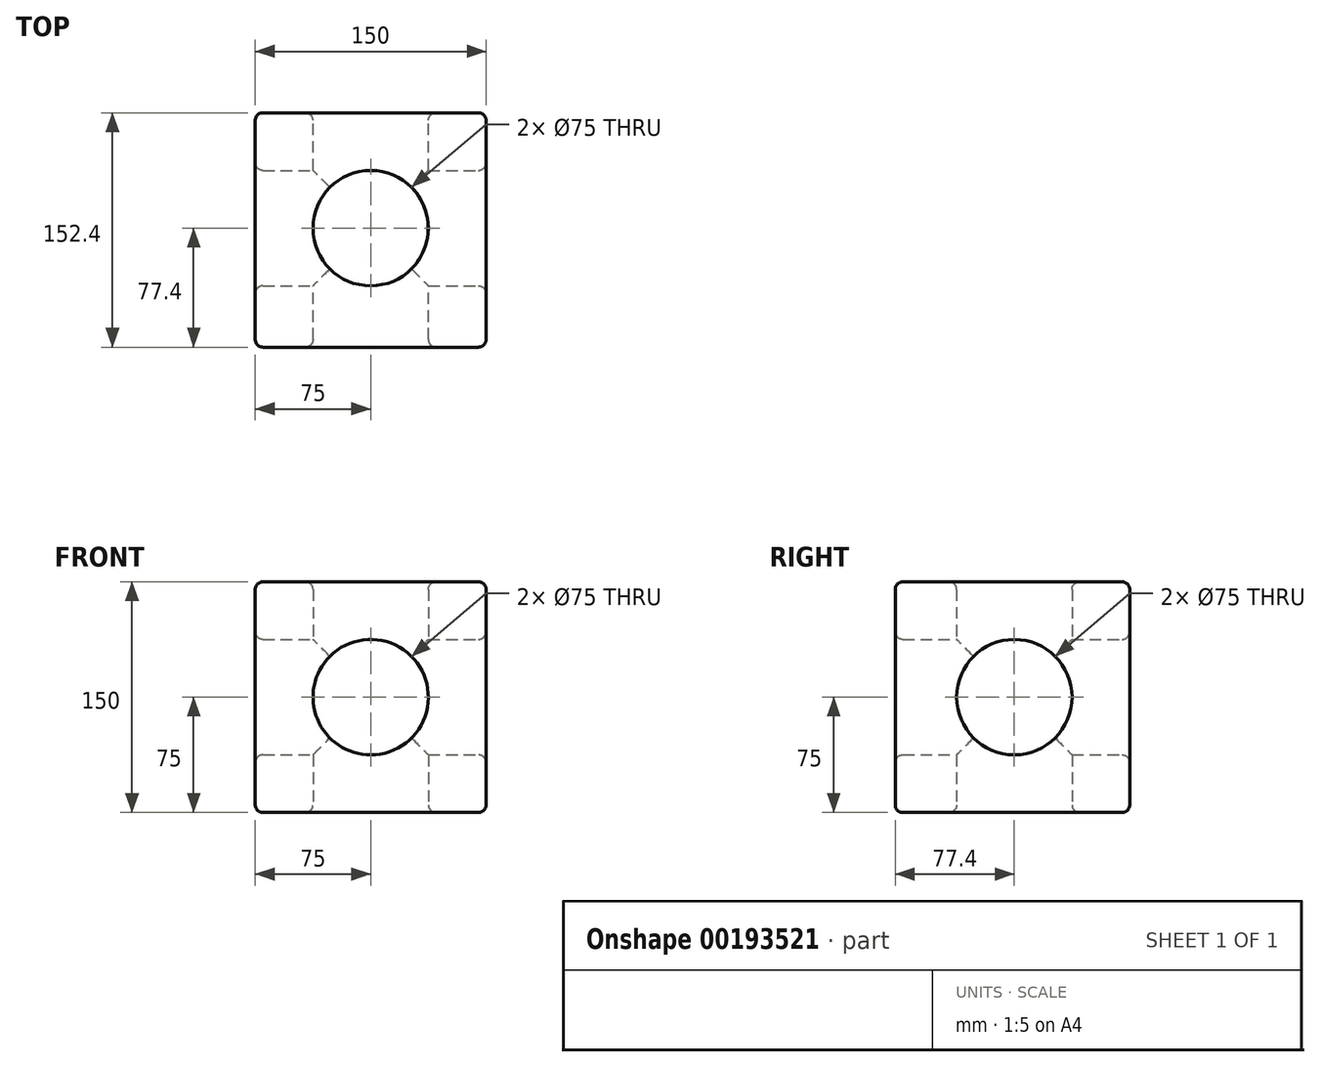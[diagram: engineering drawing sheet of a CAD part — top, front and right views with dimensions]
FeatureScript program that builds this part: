
annotation { "Feature Type Name" : "Feature", "Feature Type Description" : "" }
export const myFeature = defineFeature(function(context is Context, id is Id, definition is map)
    precondition{}
    {
        {
            var Q0;
            Q0=qCreatedBy(makeId("Front.planeOp"),FACE);
            var sketch = newSketch(context, id + "F0", { "sketchPlane" : qUnion([Q0])});
            skLineSegment(sketch, "E0.bottom", {"start": v(75, 75) * mm, "end": v(-75, 75) * mm});
            skLineSegment(sketch, "E0.top", {"start": v(75, -75) * mm, "end": v(-75, -75) * mm});
            skLineSegment(sketch, "E0.left", {"start": v(75, 75) * mm, "end": v(75, -75) * mm});
            skLineSegment(sketch, "E0.right", {"start": v(-75, 75) * mm, "end": v(-75, -75) * mm});
            skPoint(sketch, "E0.middle", {"position": v(0, 0) * mm});
            skSolve(sketch);
        }
        {
            var Q0;
            Q0=makeQuery(id+"F0.imprint","IMPRINT",FACE,{"disambiguationData":[TD([[makeQuery(id+"F0.imprint","IMPRINT",EDGE,{"derivedFrom":sQuery(id+"F0.wireOp",EDGE,"E0.bottom")}),1.0]])]});
            extrude(context, id + "F1", {"entities" : qUnion([Q0]), "depth" : 152.4 * mm});
        }
        {
            var Q0;
            Q0=makeQuery(id+"F0.imprint","IMPRINT",FACE,{"disambiguationData":[TD([[makeQuery(id+"F0.imprint","IMPRINT",EDGE,{"derivedFrom":sQuery(id+"F0.wireOp",EDGE,"E0.bottom")}),1.0]])]});
            var sketch = newSketch(context, id + "F2", { "sketchPlane" : qUnion([Q0])});
            skCircle(sketch, "E1", {"center": v(0, 0) * mm, "radius": 37.5 * mm});
            skSolve(sketch);
        }
        {
            var Q0;
            Q0 = qSketchRegion(id + "F2", true);
            extrude(context, id + "F3", {"entities" : qUnion([Q0]), "operationType" : NewBodyOperationType.REMOVE, "depth" : 252 * mm});
        }
        {
            var Q0;
            Q0=makeQuery(id+"F1.opExtrude","SWEPT_FACE",FACE,{"disambiguationData":[OSD([sQuery(id+"F0.wireOp",EDGE,"E0.top")])]});
            var sketch = newSketch(context, id + "F4", { "sketchPlane" : qUnion([Q0])});
            skCircle(sketch, "E2", {"center": v(0, 75) * mm, "radius": 37.5 * mm});
            skSolve(sketch);
        }
        {
            var Q0;
            Q0 = qSketchRegion(id + "F4", true);
            extrude(context, id + "F5", {"entities" : qUnion([Q0]), "operationType" : NewBodyOperationType.REMOVE, "oppositeDirection" : true, "depth" : 150 * mm});
        }
        {
            var Q0;
            Q0=makeQuery(id+"F1.opExtrude","SWEPT_FACE",FACE,{"disambiguationData":[OSD([sQuery(id+"F0.wireOp",EDGE,"E0.left")])]});
            var sketch = newSketch(context, id + "F6", { "sketchPlane" : qUnion([Q0])});
            skCircle(sketch, "E3", {"center": v(-75, 0) * mm, "radius": 37.5 * mm});
            skSolve(sketch);
        }
        {
            var Q0;
            Q0=makeQuery(id+"F6.imprint","IMPRINT",FACE,{"disambiguationData":[TD([[makeQuery(id+"F6.imprint","IMPRINT",EDGE,{"derivedFrom":sQuery(id+"F6.wireOp",EDGE,"E3")}),1.0]])]});
            extrude(context, id + "F7", {"entities" : qUnion([Q0]), "operationType" : NewBodyOperationType.REMOVE, "oppositeDirection" : true, "depth" : 150 * mm});
        }
        {
            var Q0;
            Q0=makeQuery(id+"F1.opExtrude","SWEPT_FACE",FACE,{"disambiguationData":[OSD([sQuery(id+"F0.wireOp",EDGE,"E0.left")])]});
            var Q1;
            Q1=makeQuery(id+"F1.opExtrude","CAP_FACE",FACE,{"disambiguationData":[OSD([sQuery(id+"F0.wireOp",EDGE,"E0.bottom"),sQuery(id+"F0.wireOp",EDGE,"E0.top"),sQuery(id+"F0.wireOp",EDGE,"E0.left"),sQuery(id+"F0.wireOp",EDGE,"E0.right")])],"isStart":false});
            var Q2;
            Q2=makeQuery(id+"F1.opExtrude","SWEPT_FACE",FACE,{"disambiguationData":[OSD([sQuery(id+"F0.wireOp",EDGE,"E0.bottom")])]});
            var Q3;
            Q3=makeQuery(id+"F1.opExtrude","SWEPT_FACE",FACE,{"disambiguationData":[OSD([sQuery(id+"F0.wireOp",EDGE,"E0.top")])]});
            var Q4;
            Q4=makeQuery(id+"F1.opExtrude","SWEPT_FACE",FACE,{"disambiguationData":[OSD([sQuery(id+"F0.wireOp",EDGE,"E0.right")])]});
            var Q5;
            Q5=makeQuery(id+"F1.opExtrude","CAP_FACE",FACE,{"disambiguationData":[OSD([sQuery(id+"F0.wireOp",EDGE,"E0.bottom"),sQuery(id+"F0.wireOp",EDGE,"E0.top"),sQuery(id+"F0.wireOp",EDGE,"E0.left"),sQuery(id+"F0.wireOp",EDGE,"E0.right")])],"isStart":true});
            var Q6;
            Q6=makeQuery(id+"F3.boolean.opBoolean","COPY",EDGE,{"derivedFrom":makeQuery(id+"F3.opExtrude","CAP_EDGE",EDGE,{"disambiguationData":[OSD([sQuery(id+"F2.wireOp",EDGE,"E1")])],"isStart":true})});
            fillet(context, id + "F8", {"entities" : qUnion([Q0, Q1, Q2, Q3, Q4, Q5, Q6]), "radius" : 5 * mm, "tangentPropagation" : true, "allowEdgeOverflow" : false});
        }
    });
